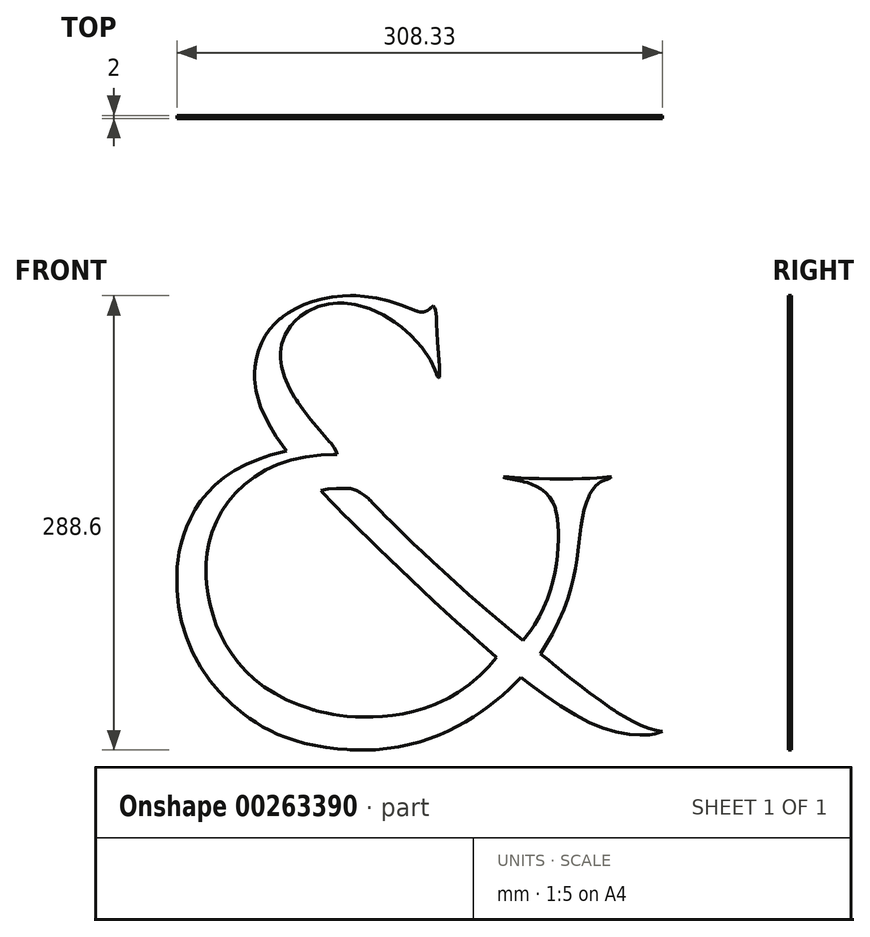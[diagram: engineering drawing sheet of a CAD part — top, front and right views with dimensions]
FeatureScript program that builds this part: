
annotation { "Feature Type Name" : "Feature", "Feature Type Description" : "" }
export const myFeature = defineFeature(function(context is Context, id is Id, definition is map)
    precondition{}
    {
        {
            var Q0;
            Q0=qCreatedBy(makeId("Front.planeOp"),FACE);
            var sketch = newSketch(context, id + "F0", { "sketchPlane" : qUnion([Q0])});
            skLineSegment(sketch, "E0.0", {"start": v(10.88, 98.57) * mm, "end": v(10.85, 99.35) * mm});
            skLineSegment(sketch, "E0.1", {"start": v(10.98, 95.31) * mm, "end": v(10.88, 98.57) * mm});
            skLineSegment(sketch, "E0.2", {"start": v(11, 93.74) * mm, "end": v(10.98, 95.31) * mm});
            skLineSegment(sketch, "E0.3", {"start": v(11, 93.23) * mm, "end": v(11, 93.74) * mm});
            skLineSegment(sketch, "E0.4", {"start": v(11, 93.13) * mm, "end": v(11, 93.23) * mm});
            skLineSegment(sketch, "E0.5", {"start": v(10.9, 92.6) * mm, "end": v(11, 93.13) * mm});
            skLineSegment(sketch, "E0.6", {"start": v(10.8, 92.45) * mm, "end": v(10.9, 92.6) * mm});
            skLineSegment(sketch, "E0.7", {"start": v(10.65, 92.35) * mm, "end": v(10.8, 92.45) * mm});
            skLineSegment(sketch, "E0.8", {"start": v(10.37, 92.3) * mm, "end": v(10.65, 92.35) * mm});
            skLineSegment(sketch, "E0.9", {"start": v(9.81, 93.06) * mm, "end": v(10.37, 92.3) * mm});
            skLineSegment(sketch, "E0.10", {"start": v(9.22, 94.33) * mm, "end": v(9.81, 93.06) * mm});
            skLineSegment(sketch, "E0.11", {"start": v(9.08, 94.75) * mm, "end": v(9.22, 94.33) * mm});
            skLineSegment(sketch, "E0.12", {"start": v(8.28, 97.07) * mm, "end": v(9.08, 94.75) * mm});
            skLineSegment(sketch, "E0.13", {"start": v(5.2, 103.48) * mm, "end": v(8.28, 97.07) * mm});
            skLineSegment(sketch, "E0.14", {"start": v(-0.18, 111.5) * mm, "end": v(5.2, 103.48) * mm});
            skLineSegment(sketch, "E0.15", {"start": v(-7.05, 118.97) * mm, "end": v(-0.18, 111.5) * mm});
            skLineSegment(sketch, "E0.16", {"start": v(-13.2, 124.31) * mm, "end": v(-7.05, 118.97) * mm});
            skLineSegment(sketch, "E0.17", {"start": v(-15.4, 125.94) * mm, "end": v(-13.2, 124.31) * mm});
            skLineSegment(sketch, "E0.18", {"start": v(-17.59, 127.57) * mm, "end": v(-15.4, 125.94) * mm});
            skLineSegment(sketch, "E0.19", {"start": v(-24.48, 131.9) * mm, "end": v(-17.59, 127.57) * mm});
            skLineSegment(sketch, "E0.20", {"start": v(-33.54, 136.2) * mm, "end": v(-24.48, 131.9) * mm});
            skLineSegment(sketch, "E0.21", {"start": v(-42.64, 138.83) * mm, "end": v(-33.54, 136.2) * mm});
            skLineSegment(sketch, "E0.22", {"start": v(-49.52, 139.73) * mm, "end": v(-42.64, 138.83) * mm});
            skLineSegment(sketch, "E0.23", {"start": v(-51.92, 139.73) * mm, "end": v(-49.52, 139.73) * mm});
            skLineSegment(sketch, "E0.24", {"start": v(-53.84, 139.73) * mm, "end": v(-51.92, 139.73) * mm});
            skLineSegment(sketch, "E0.25", {"start": v(-59.41, 139.14) * mm, "end": v(-53.84, 139.73) * mm});
            skLineSegment(sketch, "E0.26", {"start": v(-66.3, 137.37) * mm, "end": v(-59.41, 139.14) * mm});
            skLineSegment(sketch, "E0.27", {"start": v(-72.67, 134.4) * mm, "end": v(-66.3, 137.37) * mm});
            skLineSegment(sketch, "E0.28", {"start": v(-77.18, 131.36) * mm, "end": v(-72.67, 134.4) * mm});
            skLineSegment(sketch, "E0.29", {"start": v(-78.62, 130.14) * mm, "end": v(-77.18, 131.36) * mm});
            skLineSegment(sketch, "E0.30", {"start": v(-80, 128.93) * mm, "end": v(-78.62, 130.14) * mm});
            skLineSegment(sketch, "E0.31", {"start": v(-83.6, 125) * mm, "end": v(-80, 128.93) * mm});
            skLineSegment(sketch, "E0.32", {"start": v(-87.14, 119.37) * mm, "end": v(-83.6, 125) * mm});
            skLineSegment(sketch, "E0.33", {"start": v(-89.3, 113.17) * mm, "end": v(-87.14, 119.37) * mm});
            skLineSegment(sketch, "E0.34", {"start": v(-90, 108.1) * mm, "end": v(-89.3, 113.17) * mm});
            skLineSegment(sketch, "E0.35", {"start": v(-90, 106.33) * mm, "end": v(-90, 108.1) * mm});
            skLineSegment(sketch, "E0.36", {"start": v(-90, 104.52) * mm, "end": v(-90, 106.33) * mm});
            skLineSegment(sketch, "E0.37", {"start": v(-89.32, 99.47) * mm, "end": v(-90, 104.52) * mm});
            skLineSegment(sketch, "E0.38", {"start": v(-87.37, 92.57) * mm, "end": v(-89.32, 99.47) * mm});
            skLineSegment(sketch, "E0.39", {"start": v(-84.22, 85.42) * mm, "end": v(-87.37, 92.57) * mm});
            skLineSegment(sketch, "E0.40", {"start": v(-81.05, 79.78) * mm, "end": v(-84.22, 85.42) * mm});
            skLineSegment(sketch, "E0.41", {"start": v(-79.86, 77.94) * mm, "end": v(-81.05, 79.78) * mm});
            skLineSegment(sketch, "E0.42", {"start": v(-78.87, 76.43) * mm, "end": v(-79.86, 77.94) * mm});
            skLineSegment(sketch, "E0.43", {"start": v(-75.82, 72.14) * mm, "end": v(-78.87, 76.43) * mm});
            skLineSegment(sketch, "E0.44", {"start": v(-70.97, 65.81) * mm, "end": v(-75.82, 72.14) * mm});
            skLineSegment(sketch, "E0.45", {"start": v(-65.27, 58.9) * mm, "end": v(-70.97, 65.81) * mm});
            skLineSegment(sketch, "E0.46", {"start": v(-60.36, 53.25) * mm, "end": v(-65.27, 58.9) * mm});
            skLineSegment(sketch, "E0.47", {"start": v(-58.71, 51.43) * mm, "end": v(-60.36, 53.25) * mm});
            skLineSegment(sketch, "E0.48", {"start": v(-58, 50.6) * mm, "end": v(-58.71, 51.43) * mm});
            skLineSegment(sketch, "E0.49", {"start": v(-55.94, 47.76) * mm, "end": v(-58, 50.6) * mm});
            skLineSegment(sketch, "E0.50", {"start": v(-54.51, 44.91) * mm, "end": v(-55.94, 47.76) * mm});
            skLineSegment(sketch, "E0.51", {"start": v(-54.22, 43.46) * mm, "end": v(-54.51, 44.91) * mm});
            skLineSegment(sketch, "E0.52", {"start": v(-56.26, 43.49) * mm, "end": v(-54.22, 43.46) * mm});
            skLineSegment(sketch, "E0.53", {"start": v(-64.25, 43.15) * mm, "end": v(-56.26, 43.49) * mm});
            skLineSegment(sketch, "E0.54", {"start": v(-74.13, 41.94) * mm, "end": v(-64.25, 43.15) * mm});
            skLineSegment(sketch, "E0.55", {"start": v(-83.33, 39.88) * mm, "end": v(-74.13, 41.94) * mm});
            skLineSegment(sketch, "E0.56", {"start": v(-91.8, 37.03) * mm, "end": v(-83.33, 39.88) * mm});
            skLineSegment(sketch, "E0.57", {"start": v(-99.55, 33.45) * mm, "end": v(-91.8, 37.03) * mm});
            skLineSegment(sketch, "E0.58", {"start": v(-106.57, 29.22) * mm, "end": v(-99.55, 33.45) * mm});
            skLineSegment(sketch, "E0.59", {"start": v(-112.85, 24.4) * mm, "end": v(-106.57, 29.22) * mm});
            skLineSegment(sketch, "E0.60", {"start": v(-118.4, 19.1) * mm, "end": v(-112.85, 24.4) * mm});
            skLineSegment(sketch, "E0.61", {"start": v(-123.2, 13.36) * mm, "end": v(-118.4, 19.1) * mm});
            skLineSegment(sketch, "E0.62", {"start": v(-127.3, 7.27) * mm, "end": v(-123.2, 13.36) * mm});
            skLineSegment(sketch, "E0.63", {"start": v(-130.67, 0.92) * mm, "end": v(-127.3, 7.27) * mm});
            skLineSegment(sketch, "E0.64", {"start": v(-133.35, -5.63) * mm, "end": v(-130.67, 0.92) * mm});
            skLineSegment(sketch, "E0.65", {"start": v(-135.34, -12.3) * mm, "end": v(-133.35, -5.63) * mm});
            skLineSegment(sketch, "E0.66", {"start": v(-136.66, -19.03) * mm, "end": v(-135.34, -12.3) * mm});
            skLineSegment(sketch, "E0.67", {"start": v(-137.32, -25.7) * mm, "end": v(-136.66, -19.03) * mm});
            skLineSegment(sketch, "E0.68", {"start": v(-137.41, -30.7) * mm, "end": v(-137.32, -25.7) * mm});
            skLineSegment(sketch, "E0.69", {"start": v(-137.33, -32.4) * mm, "end": v(-137.41, -30.7) * mm});
            skLineSegment(sketch, "E0.70", {"start": v(-137.26, -34.04) * mm, "end": v(-137.33, -32.4) * mm});
            skLineSegment(sketch, "E0.71", {"start": v(-136.85, -38.9) * mm, "end": v(-137.26, -34.04) * mm});
            skLineSegment(sketch, "E0.72", {"start": v(-135.98, -45.36) * mm, "end": v(-136.85, -38.9) * mm});
            skLineSegment(sketch, "E0.73", {"start": v(-134.69, -51.86) * mm, "end": v(-135.98, -45.36) * mm});
            skLineSegment(sketch, "E0.74", {"start": v(-132.96, -58.32) * mm, "end": v(-134.69, -51.86) * mm});
            skLineSegment(sketch, "E0.75", {"start": v(-130.77, -64.71) * mm, "end": v(-132.96, -58.32) * mm});
            skLineSegment(sketch, "E0.76", {"start": v(-128.08, -71) * mm, "end": v(-130.77, -64.71) * mm});
            skLineSegment(sketch, "E0.77", {"start": v(-124.88, -77.12) * mm, "end": v(-128.08, -71) * mm});
            skLineSegment(sketch, "E0.78", {"start": v(-121.13, -83.06) * mm, "end": v(-124.88, -77.12) * mm});
            skLineSegment(sketch, "E0.79", {"start": v(-116.82, -88.76) * mm, "end": v(-121.13, -83.06) * mm});
            skLineSegment(sketch, "E0.80", {"start": v(-111.92, -94.2) * mm, "end": v(-116.82, -88.76) * mm});
            skLineSegment(sketch, "E0.81", {"start": v(-106.42, -99.3) * mm, "end": v(-111.92, -94.2) * mm});
            skLineSegment(sketch, "E0.82", {"start": v(-100.3, -104.05) * mm, "end": v(-106.42, -99.3) * mm});
            skLineSegment(sketch, "E0.83", {"start": v(-93.54, -108.39) * mm, "end": v(-100.3, -104.05) * mm});
            skLineSegment(sketch, "E0.84", {"start": v(-86.15, -112.3) * mm, "end": v(-93.54, -108.39) * mm});
            skLineSegment(sketch, "E0.85", {"start": v(-78.13, -115.7) * mm, "end": v(-86.15, -112.3) * mm});
            skLineSegment(sketch, "E0.86", {"start": v(-71.6, -117.99) * mm, "end": v(-78.13, -115.7) * mm});
            skLineSegment(sketch, "E0.87", {"start": v(-69.37, -118.64) * mm, "end": v(-71.6, -117.99) * mm});
            skLineSegment(sketch, "E0.88", {"start": v(-68.77, -118.82) * mm, "end": v(-69.37, -118.64) * mm});
            skLineSegment(sketch, "E0.89", {"start": v(-67, -119.3) * mm, "end": v(-68.77, -118.82) * mm});
            skLineSegment(sketch, "E0.90", {"start": v(-64.11, -120.03) * mm, "end": v(-67, -119.3) * mm});
            skLineSegment(sketch, "E0.91", {"start": v(-60.69, -120.79) * mm, "end": v(-64.11, -120.03) * mm});
            skLineSegment(sketch, "E0.92", {"start": v(-56.78, -121.52) * mm, "end": v(-60.69, -120.79) * mm});
            skLineSegment(sketch, "E0.93", {"start": v(-52.42, -122.2) * mm, "end": v(-56.78, -121.52) * mm});
            skLineSegment(sketch, "E0.94", {"start": v(-47.64, -122.76) * mm, "end": v(-52.42, -122.2) * mm});
            skLineSegment(sketch, "E0.95", {"start": v(-42.48, -123.17) * mm, "end": v(-47.64, -122.76) * mm});
            skLineSegment(sketch, "E0.96", {"start": v(-36.98, -123.38) * mm, "end": v(-42.48, -123.17) * mm});
            skLineSegment(sketch, "E0.97", {"start": v(-31.17, -123.34) * mm, "end": v(-36.98, -123.38) * mm});
            skLineSegment(sketch, "E0.98", {"start": v(-25.08, -123) * mm, "end": v(-31.17, -123.34) * mm});
            skLineSegment(sketch, "E0.99", {"start": v(-18.75, -122.31) * mm, "end": v(-25.08, -123) * mm});
            skLineSegment(sketch, "E0.100", {"start": v(-12.22, -121.24) * mm, "end": v(-18.75, -122.31) * mm});
            skLineSegment(sketch, "E0.101", {"start": v(-5.53, -119.72) * mm, "end": v(-12.22, -121.24) * mm});
            skLineSegment(sketch, "E0.102", {"start": v(1.29, -117.71) * mm, "end": v(-5.53, -119.72) * mm});
            skLineSegment(sketch, "E0.103", {"start": v(8.15, -115.18) * mm, "end": v(1.29, -117.71) * mm});
            skLineSegment(sketch, "E0.104", {"start": v(13.39, -112.9) * mm, "end": v(8.15, -115.18) * mm});
            skLineSegment(sketch, "E0.105", {"start": v(15.12, -112.04) * mm, "end": v(13.39, -112.9) * mm});
            skLineSegment(sketch, "E0.106", {"start": v(17.12, -111.06) * mm, "end": v(15.12, -112.04) * mm});
            skLineSegment(sketch, "E0.107", {"start": v(22.76, -107.77) * mm, "end": v(17.12, -111.06) * mm});
            skLineSegment(sketch, "E0.108", {"start": v(30.13, -102.6) * mm, "end": v(22.76, -107.77) * mm});
            skLineSegment(sketch, "E0.109", {"start": v(37.13, -96.55) * mm, "end": v(30.13, -102.6) * mm});
            skLineSegment(sketch, "E0.110", {"start": v(42.07, -91.48) * mm, "end": v(37.13, -96.55) * mm});
            skLineSegment(sketch, "E0.111", {"start": v(47.23, -85.34) * mm, "end": v(42.07, -91.48) * mm});
            skLineSegment(sketch, "E0.112", {"start": v(41.28, -80.18) * mm, "end": v(47.23, -85.34) * mm});
            skLineSegment(sketch, "E0.113", {"start": v(36.16, -75.67) * mm, "end": v(41.28, -80.18) * mm});
            skLineSegment(sketch, "E0.114", {"start": v(29.1, -69.4) * mm, "end": v(36.16, -75.67) * mm});
            skLineSegment(sketch, "E0.115", {"start": v(21.91, -62.9) * mm, "end": v(29.1, -69.4) * mm});
            skLineSegment(sketch, "E0.116", {"start": v(14.63, -56.26) * mm, "end": v(21.91, -62.9) * mm});
            skLineSegment(sketch, "E0.117", {"start": v(7.31, -49.5) * mm, "end": v(14.63, -56.26) * mm});
            skLineSegment(sketch, "E0.118", {"start": v(0.03, -42.72) * mm, "end": v(7.31, -49.5) * mm});
            skLineSegment(sketch, "E0.119", {"start": v(-7.17, -35.95) * mm, "end": v(0.03, -42.72) * mm});
            skLineSegment(sketch, "E0.120", {"start": v(-14.22, -29.27) * mm, "end": v(-7.17, -35.95) * mm});
            skLineSegment(sketch, "E0.121", {"start": v(-21.06, -22.73) * mm, "end": v(-14.22, -29.27) * mm});
            skLineSegment(sketch, "E0.122", {"start": v(-27.64, -16.4) * mm, "end": v(-21.06, -22.73) * mm});
            skLineSegment(sketch, "E0.123", {"start": v(-33.9, -10.32) * mm, "end": v(-27.64, -16.4) * mm});
            skLineSegment(sketch, "E0.124", {"start": v(-39.77, -4.57) * mm, "end": v(-33.9, -10.32) * mm});
            skLineSegment(sketch, "E0.125", {"start": v(-45.2, 0.8) * mm, "end": v(-39.77, -4.57) * mm});
            skLineSegment(sketch, "E0.126", {"start": v(-50.13, 5.7) * mm, "end": v(-45.2, 0.8) * mm});
            skLineSegment(sketch, "E0.127", {"start": v(-54.5, 10.12) * mm, "end": v(-50.13, 5.7) * mm});
            skLineSegment(sketch, "E0.128", {"start": v(-57.31, 13) * mm, "end": v(-54.5, 10.12) * mm});
            skLineSegment(sketch, "E0.129", {"start": v(-58.24, 13.95) * mm, "end": v(-57.31, 13) * mm});
            skLineSegment(sketch, "E0.130", {"start": v(-58.96, 14.7) * mm, "end": v(-58.24, 13.95) * mm});
            skLineSegment(sketch, "E0.131", {"start": v(-61.08, 16.96) * mm, "end": v(-58.96, 14.7) * mm});
            skLineSegment(sketch, "E0.132", {"start": v(-63.16, 19.3) * mm, "end": v(-61.08, 16.96) * mm});
            skLineSegment(sketch, "E0.133", {"start": v(-64.3, 20.7) * mm, "end": v(-63.16, 19.3) * mm});
            skLineSegment(sketch, "E0.134", {"start": v(-64.17, 20.74) * mm, "end": v(-64.3, 20.7) * mm});
            skLineSegment(sketch, "E0.135", {"start": v(-59.7, 21.46) * mm, "end": v(-64.17, 20.74) * mm});
            skLineSegment(sketch, "E0.136", {"start": v(-54.54, 21.77) * mm, "end": v(-59.7, 21.46) * mm});
            skLineSegment(sketch, "E0.137", {"start": v(-52.81, 21.8) * mm, "end": v(-54.54, 21.77) * mm});
            skLineSegment(sketch, "E0.138", {"start": v(-52.06, 21.8) * mm, "end": v(-52.81, 21.8) * mm});
            skLineSegment(sketch, "E0.139", {"start": v(-49.92, 21.86) * mm, "end": v(-52.06, 21.8) * mm});
            skLineSegment(sketch, "E0.140", {"start": v(-47.47, 21.87) * mm, "end": v(-49.92, 21.86) * mm});
            skLineSegment(sketch, "E0.141", {"start": v(-45.4, 21.73) * mm, "end": v(-47.47, 21.87) * mm});
            skLineSegment(sketch, "E0.142", {"start": v(-43.53, 21.37) * mm, "end": v(-45.4, 21.73) * mm});
            skLineSegment(sketch, "E0.143", {"start": v(-41.6, 20.68) * mm, "end": v(-43.53, 21.37) * mm});
            skLineSegment(sketch, "E0.144", {"start": v(-39.37, 19.47) * mm, "end": v(-41.6, 20.68) * mm});
            skLineSegment(sketch, "E0.145", {"start": v(-36.64, 17.5) * mm, "end": v(-39.37, 19.47) * mm});
            skLineSegment(sketch, "E0.146", {"start": v(-34.2, 15.36) * mm, "end": v(-36.64, 17.5) * mm});
            skLineSegment(sketch, "E0.147", {"start": v(-33.43, 14.62) * mm, "end": v(-34.2, 15.36) * mm});
            skLineSegment(sketch, "E0.148", {"start": v(-32.94, 14.14) * mm, "end": v(-33.43, 14.62) * mm});
            skLineSegment(sketch, "E0.149", {"start": v(-31.45, 12.65) * mm, "end": v(-32.94, 14.14) * mm});
            skLineSegment(sketch, "E0.150", {"start": v(-29.08, 10.26) * mm, "end": v(-31.45, 12.65) * mm});
            skLineSegment(sketch, "E0.151", {"start": v(-26.33, 7.45) * mm, "end": v(-29.08, 10.26) * mm});
            skLineSegment(sketch, "E0.152", {"start": v(-23.17, 4.22) * mm, "end": v(-26.33, 7.45) * mm});
            skLineSegment(sketch, "E0.153", {"start": v(-19.55, 0.56) * mm, "end": v(-23.17, 4.22) * mm});
            skLineSegment(sketch, "E0.154", {"start": v(-15.45, -3.54) * mm, "end": v(-19.55, 0.56) * mm});
            skLineSegment(sketch, "E0.155", {"start": v(-10.84, -8.08) * mm, "end": v(-15.45, -3.54) * mm});
            skLineSegment(sketch, "E0.156", {"start": v(-5.68, -13.08) * mm, "end": v(-10.84, -8.08) * mm});
            skLineSegment(sketch, "E0.157", {"start": v(0.07, -18.55) * mm, "end": v(-5.68, -13.08) * mm});
            skLineSegment(sketch, "E0.158", {"start": v(6.43, -24.5) * mm, "end": v(0.07, -18.55) * mm});
            skLineSegment(sketch, "E0.159", {"start": v(13.44, -30.93) * mm, "end": v(6.43, -24.5) * mm});
            skLineSegment(sketch, "E0.160", {"start": v(21.14, -37.87) * mm, "end": v(13.44, -30.93) * mm});
            skLineSegment(sketch, "E0.161", {"start": v(29.56, -45.32) * mm, "end": v(21.14, -37.87) * mm});
            skLineSegment(sketch, "E0.162", {"start": v(38.74, -53.3) * mm, "end": v(29.56, -45.32) * mm});
            skLineSegment(sketch, "E0.163", {"start": v(48.7, -61.8) * mm, "end": v(38.74, -53.3) * mm});
            skLineSegment(sketch, "E0.164", {"start": v(56.8, -68.62) * mm, "end": v(48.7, -61.8) * mm});
            skLineSegment(sketch, "E0.165", {"start": v(64.08, -74.69) * mm, "end": v(56.8, -68.62) * mm});
            skLineSegment(sketch, "E0.166", {"start": v(68.66, -68.66) * mm, "end": v(64.08, -74.69) * mm});
            skLineSegment(sketch, "E0.167", {"start": v(71.3, -64.77) * mm, "end": v(68.66, -68.66) * mm});
            skLineSegment(sketch, "E0.168", {"start": v(74.42, -59.44) * mm, "end": v(71.3, -64.77) * mm});
            skLineSegment(sketch, "E0.169", {"start": v(77.14, -53.93) * mm, "end": v(74.42, -59.44) * mm});
            skLineSegment(sketch, "E0.170", {"start": v(79.45, -48.33) * mm, "end": v(77.14, -53.93) * mm});
            skLineSegment(sketch, "E0.171", {"start": v(81.4, -42.67) * mm, "end": v(79.45, -48.33) * mm});
            skLineSegment(sketch, "E0.172", {"start": v(82.98, -37.03) * mm, "end": v(81.4, -42.67) * mm});
            skLineSegment(sketch, "E0.173", {"start": v(84.25, -31.43) * mm, "end": v(82.98, -37.03) * mm});
            skLineSegment(sketch, "E0.174", {"start": v(85.21, -25.93) * mm, "end": v(84.25, -31.43) * mm});
            skLineSegment(sketch, "E0.175", {"start": v(85.9, -20.58) * mm, "end": v(85.21, -25.93) * mm});
            skLineSegment(sketch, "E0.176", {"start": v(86.32, -15.42) * mm, "end": v(85.9, -20.58) * mm});
            skLineSegment(sketch, "E0.177", {"start": v(86.51, -10.5) * mm, "end": v(86.32, -15.42) * mm});
            skLineSegment(sketch, "E0.178", {"start": v(86.49, -5.87) * mm, "end": v(86.51, -10.5) * mm});
            skLineSegment(sketch, "E0.179", {"start": v(86.26, -1.55) * mm, "end": v(86.49, -5.87) * mm});
            skLineSegment(sketch, "E0.180", {"start": v(85.85, 2.4) * mm, "end": v(86.26, -1.55) * mm});
            skLineSegment(sketch, "E0.181", {"start": v(85.28, 5.95) * mm, "end": v(85.85, 2.4) * mm});
            skLineSegment(sketch, "E0.182", {"start": v(84.75, 8.32) * mm, "end": v(85.28, 5.95) * mm});
            skLineSegment(sketch, "E0.183", {"start": v(84.51, 9.14) * mm, "end": v(84.75, 8.32) * mm});
            skLineSegment(sketch, "E0.184", {"start": v(84.2, 10.22) * mm, "end": v(84.51, 9.14) * mm});
            skLineSegment(sketch, "E0.185", {"start": v(82.98, 13.1) * mm, "end": v(84.2, 10.22) * mm});
            skLineSegment(sketch, "E0.186", {"start": v(80.91, 16.38) * mm, "end": v(82.98, 13.1) * mm});
            skLineSegment(sketch, "E0.187", {"start": v(78.38, 19.17) * mm, "end": v(80.91, 16.38) * mm});
            skLineSegment(sketch, "E0.188", {"start": v(75.58, 21.41) * mm, "end": v(78.38, 19.17) * mm});
            skLineSegment(sketch, "E0.189", {"start": v(72.65, 23.18) * mm, "end": v(75.58, 21.41) * mm});
            skLineSegment(sketch, "E0.190", {"start": v(69.7, 24.54) * mm, "end": v(72.65, 23.18) * mm});
            skLineSegment(sketch, "E0.191", {"start": v(66.84, 25.53) * mm, "end": v(69.7, 24.54) * mm});
            skLineSegment(sketch, "E0.192", {"start": v(64.76, 26.08) * mm, "end": v(66.84, 25.53) * mm});
            skLineSegment(sketch, "E0.193", {"start": v(63.98, 26.25) * mm, "end": v(64.76, 26.08) * mm});
            skLineSegment(sketch, "E0.194", {"start": v(54.4, 28.1) * mm, "end": v(63.98, 26.25) * mm});
            skLineSegment(sketch, "E0.195", {"start": v(54.07, 28.16) * mm, "end": v(54.4, 28.1) * mm});
            skLineSegment(sketch, "E0.196", {"start": v(52.96, 28.48) * mm, "end": v(54.07, 28.16) * mm});
            skLineSegment(sketch, "E0.197", {"start": v(52, 28.91) * mm, "end": v(52.96, 28.48) * mm});
            skLineSegment(sketch, "E0.198", {"start": v(51.6, 29.2) * mm, "end": v(52, 28.91) * mm});
            skLineSegment(sketch, "E0.199", {"start": v(52.17, 29.26) * mm, "end": v(51.6, 29.2) * mm});
            skLineSegment(sketch, "E0.200", {"start": v(52.38, 29.26) * mm, "end": v(52.17, 29.26) * mm});
            skLineSegment(sketch, "E0.201", {"start": v(52.46, 29.26) * mm, "end": v(52.38, 29.26) * mm});
            skLineSegment(sketch, "E0.202", {"start": v(53.11, 29.21) * mm, "end": v(52.46, 29.26) * mm});
            skLineSegment(sketch, "E0.203", {"start": v(55.28, 29.06) * mm, "end": v(53.11, 29.21) * mm});
            skLineSegment(sketch, "E0.204", {"start": v(58.48, 28.83) * mm, "end": v(55.28, 29.06) * mm});
            skLineSegment(sketch, "E0.205", {"start": v(62.7, 28.56) * mm, "end": v(58.48, 28.83) * mm});
            skLineSegment(sketch, "E0.206", {"start": v(67.91, 28.3) * mm, "end": v(62.7, 28.56) * mm});
            skLineSegment(sketch, "E0.207", {"start": v(74.12, 28.07) * mm, "end": v(67.91, 28.3) * mm});
            skLineSegment(sketch, "E0.208", {"start": v(81.3, 27.9) * mm, "end": v(74.12, 28.07) * mm});
            skLineSegment(sketch, "E0.209", {"start": v(-86.43, -136.35) * mm, "end": v(-80.75, -138.26) * mm});
            skLineSegment(sketch, "E0.210", {"start": v(-91.73, -134.24) * mm, "end": v(-86.43, -136.35) * mm});
            skLineSegment(sketch, "E0.211", {"start": v(-96.69, -131.94) * mm, "end": v(-91.73, -134.24) * mm});
            skLineSegment(sketch, "E0.212", {"start": v(-101.32, -129.48) * mm, "end": v(-96.69, -131.94) * mm});
            skLineSegment(sketch, "E0.213", {"start": v(-105.67, -126.86) * mm, "end": v(-101.32, -129.48) * mm});
            skLineSegment(sketch, "E0.214", {"start": v(-109.76, -124.12) * mm, "end": v(-105.67, -126.86) * mm});
            skLineSegment(sketch, "E0.215", {"start": v(-113.61, -121.26) * mm, "end": v(-109.76, -124.12) * mm});
            skLineSegment(sketch, "E0.216", {"start": v(-117.26, -118.3) * mm, "end": v(-113.61, -121.26) * mm});
            skLineSegment(sketch, "E0.217", {"start": v(-120.72, -115.24) * mm, "end": v(-117.26, -118.3) * mm});
            skLineSegment(sketch, "E0.218", {"start": v(-124.04, -112.11) * mm, "end": v(-120.72, -115.24) * mm});
            skLineSegment(sketch, "E0.219", {"start": v(-126.43, -109.75) * mm, "end": v(-124.04, -112.11) * mm});
            skLineSegment(sketch, "E0.220", {"start": v(-127.2, -108.95) * mm, "end": v(-126.43, -109.75) * mm});
            skLineSegment(sketch, "E0.221", {"start": v(-129.13, -106.97) * mm, "end": v(-127.2, -108.95) * mm});
            skLineSegment(sketch, "E0.222", {"start": v(-134.6, -100.5) * mm, "end": v(-129.13, -106.97) * mm});
            skLineSegment(sketch, "E0.223", {"start": v(-140.82, -91.6) * mm, "end": v(-134.6, -100.5) * mm});
            skLineSegment(sketch, "E0.224", {"start": v(-145.85, -82.36) * mm, "end": v(-140.82, -91.6) * mm});
            skLineSegment(sketch, "E0.225", {"start": v(-149.79, -72.82) * mm, "end": v(-145.85, -82.36) * mm});
            skLineSegment(sketch, "E0.226", {"start": v(-152.7, -63) * mm, "end": v(-149.79, -72.82) * mm});
            skLineSegment(sketch, "E0.227", {"start": v(-154.62, -52.94) * mm, "end": v(-152.7, -63) * mm});
            skLineSegment(sketch, "E0.228", {"start": v(-155.63, -42.65) * mm, "end": v(-154.62, -52.94) * mm});
            skLineSegment(sketch, "E0.229", {"start": v(-155.83, -34.86) * mm, "end": v(-155.63, -42.65) * mm});
            skLineSegment(sketch, "E0.230", {"start": v(-155.75, -32.3) * mm, "end": v(-155.83, -34.86) * mm});
            skLineSegment(sketch, "E0.231", {"start": v(-155.73, -31.26) * mm, "end": v(-155.75, -32.3) * mm});
            skLineSegment(sketch, "E0.232", {"start": v(-155.54, -28.12) * mm, "end": v(-155.73, -31.26) * mm});
            skLineSegment(sketch, "E0.233", {"start": v(-155.06, -23.5) * mm, "end": v(-155.54, -28.12) * mm});
            skLineSegment(sketch, "E0.234", {"start": v(-154.3, -18.57) * mm, "end": v(-155.06, -23.5) * mm});
            skLineSegment(sketch, "E0.235", {"start": v(-153.17, -13.38) * mm, "end": v(-154.3, -18.57) * mm});
            skLineSegment(sketch, "E0.236", {"start": v(-151.66, -8.02) * mm, "end": v(-153.17, -13.38) * mm});
            skLineSegment(sketch, "E0.237", {"start": v(-149.7, -2.55) * mm, "end": v(-151.66, -8.02) * mm});
            skLineSegment(sketch, "E0.238", {"start": v(-147.23, 2.96) * mm, "end": v(-149.7, -2.55) * mm});
            skLineSegment(sketch, "E0.239", {"start": v(-144.24, 8.43) * mm, "end": v(-147.23, 2.96) * mm});
            skLineSegment(sketch, "E0.240", {"start": v(-140.65, 13.8) * mm, "end": v(-144.24, 8.43) * mm});
            skLineSegment(sketch, "E0.241", {"start": v(-136.42, 19.03) * mm, "end": v(-140.65, 13.8) * mm});
            skLineSegment(sketch, "E0.242", {"start": v(-131.48, 24.03) * mm, "end": v(-136.42, 19.03) * mm});
            skLineSegment(sketch, "E0.243", {"start": v(-125.8, 28.76) * mm, "end": v(-131.48, 24.03) * mm});
            skLineSegment(sketch, "E0.244", {"start": v(-119.27, 33.15) * mm, "end": v(-125.8, 28.76) * mm});
            skLineSegment(sketch, "E0.245", {"start": v(-111.86, 37.13) * mm, "end": v(-119.27, 33.15) * mm});
            skLineSegment(sketch, "E0.246", {"start": v(-103.44, 40.66) * mm, "end": v(-111.86, 37.13) * mm});
            skLineSegment(sketch, "E0.247", {"start": v(-96.4, 42.98) * mm, "end": v(-103.44, 40.66) * mm});
            skLineSegment(sketch, "E0.248", {"start": v(-86, 45.75) * mm, "end": v(-96.4, 42.98) * mm});
            skLineSegment(sketch, "E0.249", {"start": v(-92.77, 54.99) * mm, "end": v(-86, 45.75) * mm});
            skLineSegment(sketch, "E0.250", {"start": v(-97.74, 63.1) * mm, "end": v(-92.77, 54.99) * mm});
            skLineSegment(sketch, "E0.251", {"start": v(-102.56, 73.6) * mm, "end": v(-97.74, 63.1) * mm});
            skLineSegment(sketch, "E0.252", {"start": v(-105.42, 83.9) * mm, "end": v(-102.56, 73.6) * mm});
            skLineSegment(sketch, "E0.253", {"start": v(-106.35, 91.42) * mm, "end": v(-105.42, 83.9) * mm});
            skLineSegment(sketch, "E0.254", {"start": v(-106.35, 93.83) * mm, "end": v(-106.35, 91.42) * mm});
            skLineSegment(sketch, "E0.255", {"start": v(-106.35, 95.19) * mm, "end": v(-106.35, 93.83) * mm});
            skLineSegment(sketch, "E0.256", {"start": v(-106.08, 99.38) * mm, "end": v(-106.35, 95.19) * mm});
            skLineSegment(sketch, "E0.257", {"start": v(-105.27, 104.7) * mm, "end": v(-106.08, 99.38) * mm});
            skLineSegment(sketch, "E0.258", {"start": v(-103.95, 109.64) * mm, "end": v(-105.27, 104.7) * mm});
            skLineSegment(sketch, "E0.259", {"start": v(-2.63, 134.2) * mm, "end": v(-3.42, 134.44) * mm});
            skLineSegment(sketch, "E0.260", {"start": v(-1.47, 133.96) * mm, "end": v(-2.63, 134.2) * mm});
            skLineSegment(sketch, "E0.261", {"start": v(-0.1, 133.86) * mm, "end": v(-1.47, 133.96) * mm});
            skLineSegment(sketch, "E0.262", {"start": v(0.7, 133.96) * mm, "end": v(-0.1, 133.86) * mm});
            skLineSegment(sketch, "E0.263", {"start": v(1.83, 134.14) * mm, "end": v(0.7, 133.96) * mm});
            skLineSegment(sketch, "E0.264", {"start": v(3.45, 135) * mm, "end": v(1.83, 134.14) * mm});
            skLineSegment(sketch, "E0.265", {"start": v(4.6, 135.85) * mm, "end": v(3.45, 135) * mm});
            skLineSegment(sketch, "E0.266", {"start": v(5.44, 136.56) * mm, "end": v(4.6, 135.85) * mm});
            skLineSegment(sketch, "E0.267", {"start": v(5.84, 136.9) * mm, "end": v(5.44, 136.56) * mm});
            skLineSegment(sketch, "E0.268", {"start": v(5.92, 136.96) * mm, "end": v(5.84, 136.9) * mm});
            skLineSegment(sketch, "E0.269", {"start": v(6.08, 137.09) * mm, "end": v(5.92, 136.96) * mm});
            skLineSegment(sketch, "E0.270", {"start": v(6.65, 137.48) * mm, "end": v(6.08, 137.09) * mm});
            skLineSegment(sketch, "E0.271", {"start": v(9.18, 128.45) * mm, "end": v(9.08, 130.67) * mm});
            skLineSegment(sketch, "E0.272", {"start": v(9.19, 127.13) * mm, "end": v(9.18, 128.45) * mm});
            skLineSegment(sketch, "E0.273", {"start": v(9.19, 126.52) * mm, "end": v(9.19, 127.13) * mm});
            skLineSegment(sketch, "E0.274", {"start": v(9.82, 115.32) * mm, "end": v(9.19, 126.52) * mm});
            skLineSegment(sketch, "E0.275", {"start": v(9.08, 130.67) * mm, "end": v(8.84, 133) * mm});
            skLineSegment(sketch, "E0.276", {"start": v(8.84, 133) * mm, "end": v(8.41, 135.17) * mm});
            skLineSegment(sketch, "E0.277", {"start": v(8.41, 135.17) * mm, "end": v(7.84, 136.8) * mm});
            skLineSegment(sketch, "E0.278", {"start": v(7.84, 136.8) * mm, "end": v(7.34, 137.6) * mm});
            skLineSegment(sketch, "E0.279", {"start": v(7.34, 137.6) * mm, "end": v(7.16, 137.74) * mm});
            skLineSegment(sketch, "E0.280", {"start": v(7.16, 137.74) * mm, "end": v(6.65, 137.48) * mm});
            skLineSegment(sketch, "E0.281", {"start": v(-3.42, 134.44) * mm, "end": v(-3.76, 134.57) * mm});
            skLineSegment(sketch, "E0.282", {"start": v(-3.76, 134.57) * mm, "end": v(-13.38, 138.25) * mm});
            skLineSegment(sketch, "E0.283", {"start": v(-13.38, 138.25) * mm, "end": v(-15.29, 138.98) * mm});
            skLineSegment(sketch, "E0.284", {"start": v(-15.29, 138.98) * mm, "end": v(-21.22, 140.89) * mm});
            skLineSegment(sketch, "E0.285", {"start": v(-21.22, 140.89) * mm, "end": v(-28.96, 142.78) * mm});
            skLineSegment(sketch, "E0.286", {"start": v(-28.96, 142.78) * mm, "end": v(-36.5, 143.92) * mm});
            skLineSegment(sketch, "E0.287", {"start": v(-36.5, 143.92) * mm, "end": v(-41.94, 144.3) * mm});
            skLineSegment(sketch, "E0.288", {"start": v(-41.94, 144.3) * mm, "end": v(-43.7, 144.3) * mm});
            skLineSegment(sketch, "E0.289", {"start": v(-43.7, 144.3) * mm, "end": v(-45.43, 144.3) * mm});
            skLineSegment(sketch, "E0.290", {"start": v(-45.43, 144.3) * mm, "end": v(-50.7, 144.07) * mm});
            skLineSegment(sketch, "E0.291", {"start": v(-50.7, 144.07) * mm, "end": v(-57.4, 143.39) * mm});
            skLineSegment(sketch, "E0.292", {"start": v(-57.4, 143.39) * mm, "end": v(-63.7, 142.26) * mm});
            skLineSegment(sketch, "E0.293", {"start": v(-63.7, 142.26) * mm, "end": v(-69.6, 140.7) * mm});
            skLineSegment(sketch, "E0.294", {"start": v(-69.6, 140.7) * mm, "end": v(-75.12, 138.71) * mm});
            skLineSegment(sketch, "E0.295", {"start": v(-75.12, 138.71) * mm, "end": v(-80.27, 136.3) * mm});
            skLineSegment(sketch, "E0.296", {"start": v(-80.27, 136.3) * mm, "end": v(-85.1, 133.45) * mm});
            skLineSegment(sketch, "E0.297", {"start": v(-85.1, 133.45) * mm, "end": v(-88.45, 131.08) * mm});
            skLineSegment(sketch, "E0.298", {"start": v(-88.45, 131.08) * mm, "end": v(-89.47, 130.25) * mm});
            skLineSegment(sketch, "E0.299", {"start": v(-89.47, 130.25) * mm, "end": v(-90.47, 129.43) * mm});
            skLineSegment(sketch, "E0.300", {"start": v(-90.47, 129.43) * mm, "end": v(-93.42, 126.66) * mm});
            skLineSegment(sketch, "E0.301", {"start": v(-93.42, 126.66) * mm, "end": v(-96.88, 122.76) * mm});
            skLineSegment(sketch, "E0.302", {"start": v(-96.88, 122.76) * mm, "end": v(-99.76, 118.65) * mm});
            skLineSegment(sketch, "E0.303", {"start": v(-99.76, 118.65) * mm, "end": v(-102.11, 114.29) * mm});
            skLineSegment(sketch, "E0.304", {"start": v(-102.11, 114.29) * mm, "end": v(-103.95, 109.64) * mm});
            skLineSegment(sketch, "E0.305", {"start": v(-80.75, -138.26) * mm, "end": v(-74.67, -139.96) * mm});
            skLineSegment(sketch, "E0.306", {"start": v(-74.67, -139.96) * mm, "end": v(-68.15, -141.4) * mm});
            skLineSegment(sketch, "E0.307", {"start": v(-68.15, -141.4) * mm, "end": v(-61.17, -142.6) * mm});
            skLineSegment(sketch, "E0.308", {"start": v(-61.17, -142.6) * mm, "end": v(-53.68, -143.5) * mm});
            skLineSegment(sketch, "E0.309", {"start": v(10.85, 99.35) * mm, "end": v(9.82, 115.32) * mm});
            skLineSegment(sketch, "E0.310", {"start": v(-53.68, -143.5) * mm, "end": v(-47.7, -143.99) * mm});
            skLineSegment(sketch, "E0.311", {"start": v(-47.7, -143.99) * mm, "end": v(-45.71, -144.1) * mm});
            skLineSegment(sketch, "E0.312", {"start": v(-45.71, -144.1) * mm, "end": v(-43.7, -144.2) * mm});
            skLineSegment(sketch, "E0.313", {"start": v(-43.7, -144.2) * mm, "end": v(-37.59, -144.3) * mm});
            skLineSegment(sketch, "E0.314", {"start": v(-37.59, -144.3) * mm, "end": v(-29.73, -144.04) * mm});
            skLineSegment(sketch, "E0.315", {"start": v(-29.73, -144.04) * mm, "end": v(-22.23, -143.36) * mm});
            skLineSegment(sketch, "E0.316", {"start": v(-22.23, -143.36) * mm, "end": v(-15.03, -142.28) * mm});
            skLineSegment(sketch, "E0.317", {"start": v(-15.03, -142.28) * mm, "end": v(-8.13, -140.84) * mm});
            skLineSegment(sketch, "E0.318", {"start": v(-8.13, -140.84) * mm, "end": v(-1.52, -139.07) * mm});
            skLineSegment(sketch, "E0.319", {"start": v(-1.52, -139.07) * mm, "end": v(4.82, -137) * mm});
            skLineSegment(sketch, "E0.320", {"start": v(4.82, -137) * mm, "end": v(10.89, -134.65) * mm});
            skLineSegment(sketch, "E0.321", {"start": v(10.89, -134.65) * mm, "end": v(16.7, -132.06) * mm});
            skLineSegment(sketch, "E0.322", {"start": v(16.7, -132.06) * mm, "end": v(22.25, -129.26) * mm});
            skLineSegment(sketch, "E0.323", {"start": v(22.25, -129.26) * mm, "end": v(27.56, -126.28) * mm});
            skLineSegment(sketch, "E0.324", {"start": v(27.56, -126.28) * mm, "end": v(32.63, -123.16) * mm});
            skLineSegment(sketch, "E0.325", {"start": v(32.63, -123.16) * mm, "end": v(37.47, -119.91) * mm});
            skLineSegment(sketch, "E0.326", {"start": v(37.47, -119.91) * mm, "end": v(42.09, -116.58) * mm});
            skLineSegment(sketch, "E0.327", {"start": v(42.09, -116.58) * mm, "end": v(46.5, -113.18) * mm});
            skLineSegment(sketch, "E0.328", {"start": v(46.5, -113.18) * mm, "end": v(49.64, -110.64) * mm});
            skLineSegment(sketch, "E0.329", {"start": v(49.64, -110.64) * mm, "end": v(50.67, -109.77) * mm});
            skLineSegment(sketch, "E0.330", {"start": v(50.67, -109.77) * mm, "end": v(51.08, -109.43) * mm});
            skLineSegment(sketch, "E0.331", {"start": v(51.08, -109.43) * mm, "end": v(52.34, -108.32) * mm});
            skLineSegment(sketch, "E0.332", {"start": v(52.34, -108.32) * mm, "end": v(54.4, -106.44) * mm});
            skLineSegment(sketch, "E0.333", {"start": v(54.4, -106.44) * mm, "end": v(56.73, -104.21) * mm});
            skLineSegment(sketch, "E0.334", {"start": v(56.73, -104.21) * mm, "end": v(58.65, -102.34) * mm});
            skLineSegment(sketch, "E0.335", {"start": v(58.65, -102.34) * mm, "end": v(62.78, -98.22) * mm});
            skLineSegment(sketch, "E0.336", {"start": v(62.78, -98.22) * mm, "end": v(69.45, -103.23) * mm});
            skLineSegment(sketch, "E0.337", {"start": v(69.45, -103.23) * mm, "end": v(77.72, -109.25) * mm});
            skLineSegment(sketch, "E0.338", {"start": v(77.72, -109.25) * mm, "end": v(87.82, -116.2) * mm});
            skLineSegment(sketch, "E0.339", {"start": v(87.82, -116.2) * mm, "end": v(97.2, -121.98) * mm});
            skLineSegment(sketch, "E0.340", {"start": v(97.2, -121.98) * mm, "end": v(106.05, -126.64) * mm});
            skLineSegment(sketch, "E0.341", {"start": v(106.05, -126.64) * mm, "end": v(114.56, -130.2) * mm});
            skLineSegment(sketch, "E0.342", {"start": v(114.56, -130.2) * mm, "end": v(122.97, -132.72) * mm});
            skLineSegment(sketch, "E0.343", {"start": v(122.97, -132.72) * mm, "end": v(131.58, -134.23) * mm});
            skLineSegment(sketch, "E0.344", {"start": v(131.58, -134.23) * mm, "end": v(138.3, -134.73) * mm});
            skLineSegment(sketch, "E0.345", {"start": v(138.3, -134.73) * mm, "end": v(140.5, -134.73) * mm});
            skLineSegment(sketch, "E0.346", {"start": v(140.5, -134.73) * mm, "end": v(141.46, -134.73) * mm});
            skLineSegment(sketch, "E0.347", {"start": v(141.46, -134.73) * mm, "end": v(144.47, -134.53) * mm});
            skLineSegment(sketch, "E0.348", {"start": v(144.47, -134.53) * mm, "end": v(147.93, -133.98) * mm});
            skLineSegment(sketch, "E0.349", {"start": v(147.93, -133.98) * mm, "end": v(150.72, -133.2) * mm});
            skLineSegment(sketch, "E0.350", {"start": v(150.72, -133.2) * mm, "end": v(152.5, -132.43) * mm});
            skLineSegment(sketch, "E0.351", {"start": v(152.5, -132.43) * mm, "end": v(148.75, -131.8) * mm});
            skLineSegment(sketch, "E0.352", {"start": v(148.75, -131.8) * mm, "end": v(144.04, -130.5) * mm});
            skLineSegment(sketch, "E0.353", {"start": v(144.04, -130.5) * mm, "end": v(139.05, -128.61) * mm});
            skLineSegment(sketch, "E0.354", {"start": v(139.05, -128.61) * mm, "end": v(133.76, -126.14) * mm});
            skLineSegment(sketch, "E0.355", {"start": v(133.76, -126.14) * mm, "end": v(128.19, -123.04) * mm});
            skLineSegment(sketch, "E0.356", {"start": v(128.19, -123.04) * mm, "end": v(123.72, -120.24) * mm});
            skLineSegment(sketch, "E0.357", {"start": v(123.72, -120.24) * mm, "end": v(122.25, -119.25) * mm});
            skLineSegment(sketch, "E0.358", {"start": v(122.25, -119.25) * mm, "end": v(120.03, -117.74) * mm});
            skLineSegment(sketch, "E0.359", {"start": v(120.03, -117.74) * mm, "end": v(113.45, -113.17) * mm});
            skLineSegment(sketch, "E0.360", {"start": v(113.45, -113.17) * mm, "end": v(106.17, -107.93) * mm});
            skLineSegment(sketch, "E0.361", {"start": v(106.17, -107.93) * mm, "end": v(100.1, -103.38) * mm});
            skLineSegment(sketch, "E0.362", {"start": v(100.1, -103.38) * mm, "end": v(95, -99.37) * mm});
            skLineSegment(sketch, "E0.363", {"start": v(95, -99.37) * mm, "end": v(90.63, -95.8) * mm});
            skLineSegment(sketch, "E0.364", {"start": v(90.63, -95.8) * mm, "end": v(86.71, -92.54) * mm});
            skLineSegment(sketch, "E0.365", {"start": v(86.71, -92.54) * mm, "end": v(83, -89.46) * mm});
            skLineSegment(sketch, "E0.366", {"start": v(83, -89.46) * mm, "end": v(80.16, -87.16) * mm});
            skLineSegment(sketch, "E0.367", {"start": v(80.16, -87.16) * mm, "end": v(75.26, -83.32) * mm});
            skLineSegment(sketch, "E0.368", {"start": v(75.26, -83.32) * mm, "end": v(79.1, -76.93) * mm});
            skLineSegment(sketch, "E0.369", {"start": v(79.1, -76.93) * mm, "end": v(82.66, -70.52) * mm});
            skLineSegment(sketch, "E0.370", {"start": v(82.66, -70.52) * mm, "end": v(86.66, -62.51) * mm});
            skLineSegment(sketch, "E0.371", {"start": v(86.66, -62.51) * mm, "end": v(89.9, -55.01) * mm});
            skLineSegment(sketch, "E0.372", {"start": v(89.9, -55.01) * mm, "end": v(92.5, -47.96) * mm});
            skLineSegment(sketch, "E0.373", {"start": v(92.5, -47.96) * mm, "end": v(94.54, -41.31) * mm});
            skLineSegment(sketch, "E0.374", {"start": v(94.54, -41.31) * mm, "end": v(96.13, -35.02) * mm});
            skLineSegment(sketch, "E0.375", {"start": v(96.13, -35.02) * mm, "end": v(97.34, -29.04) * mm});
            skLineSegment(sketch, "E0.376", {"start": v(97.34, -29.04) * mm, "end": v(98.27, -23.33) * mm});
            skLineSegment(sketch, "E0.377", {"start": v(98.27, -23.33) * mm, "end": v(99, -17.82) * mm});
            skLineSegment(sketch, "E0.378", {"start": v(99, -17.82) * mm, "end": v(99.63, -12.48) * mm});
            skLineSegment(sketch, "E0.379", {"start": v(99.63, -12.48) * mm, "end": v(100.24, -7.26) * mm});
            skLineSegment(sketch, "E0.380", {"start": v(100.24, -7.26) * mm, "end": v(100.92, -2.12) * mm});
            skLineSegment(sketch, "E0.381", {"start": v(100.92, -2.12) * mm, "end": v(101.78, 2.98) * mm});
            skLineSegment(sketch, "E0.382", {"start": v(101.78, 2.98) * mm, "end": v(102.91, 8.06) * mm});
            skLineSegment(sketch, "E0.383", {"start": v(102.91, 8.06) * mm, "end": v(104.41, 13.1) * mm});
            skLineSegment(sketch, "E0.384", {"start": v(104.41, 13.1) * mm, "end": v(105.85, 16.93) * mm});
            skLineSegment(sketch, "E0.385", {"start": v(105.85, 16.93) * mm, "end": v(106.42, 18.2) * mm});
            skLineSegment(sketch, "E0.386", {"start": v(106.42, 18.2) * mm, "end": v(106.77, 18.98) * mm});
            skLineSegment(sketch, "E0.387", {"start": v(106.77, 18.98) * mm, "end": v(108.01, 21.06) * mm});
            skLineSegment(sketch, "E0.388", {"start": v(108.01, 21.06) * mm, "end": v(110.27, 23.64) * mm});
            skLineSegment(sketch, "E0.389", {"start": v(110.27, 23.64) * mm, "end": v(113.32, 25.87) * mm});
            skLineSegment(sketch, "E0.390", {"start": v(113.32, 25.87) * mm, "end": v(116.23, 27.32) * mm});
            skLineSegment(sketch, "E0.391", {"start": v(116.23, 27.32) * mm, "end": v(117.32, 27.72) * mm});
            skLineSegment(sketch, "E0.392", {"start": v(117.32, 27.72) * mm, "end": v(117.87, 27.92) * mm});
            skLineSegment(sketch, "E0.393", {"start": v(117.87, 27.92) * mm, "end": v(119.4, 28.66) * mm});
            skLineSegment(sketch, "E0.394", {"start": v(119.4, 28.66) * mm, "end": v(120.18, 29.26) * mm});
            skLineSegment(sketch, "E0.395", {"start": v(120.18, 29.26) * mm, "end": v(120.14, 29.26) * mm});
            skLineSegment(sketch, "E0.396", {"start": v(120.14, 29.26) * mm, "end": v(120.04, 29.26) * mm});
            skLineSegment(sketch, "E0.397", {"start": v(120.04, 29.26) * mm, "end": v(119.38, 29.21) * mm});
            skLineSegment(sketch, "E0.398", {"start": v(119.38, 29.21) * mm, "end": v(117.41, 29.06) * mm});
            skLineSegment(sketch, "E0.399", {"start": v(117.41, 29.06) * mm, "end": v(114.6, 28.83) * mm});
            skLineSegment(sketch, "E0.400", {"start": v(114.6, 28.83) * mm, "end": v(110.98, 28.56) * mm});
            skLineSegment(sketch, "E0.401", {"start": v(110.98, 28.56) * mm, "end": v(106.62, 28.3) * mm});
            skLineSegment(sketch, "E0.402", {"start": v(106.62, 28.3) * mm, "end": v(101.56, 28.07) * mm});
            skLineSegment(sketch, "E0.403", {"start": v(101.56, 28.07) * mm, "end": v(95.84, 27.9) * mm});
            skLineSegment(sketch, "E0.404", {"start": v(95.84, 27.9) * mm, "end": v(91.06, 27.84) * mm});
            skLineSegment(sketch, "E0.405", {"start": v(91.06, 27.84) * mm, "end": v(89.46, 27.84) * mm});
            skLineSegment(sketch, "E0.406", {"start": v(89.46, 27.84) * mm, "end": v(87.41, 27.84) * mm});
            skLineSegment(sketch, "E0.407", {"start": v(87.41, 27.84) * mm, "end": v(81.3, 27.9) * mm});
            skSolve(sketch);
        }
        {
            var Q0;
            Q0=makeQuery(id+"F0.imprint","IMPRINT",FACE,{"disambiguationData":[TD([[makeQuery(id+"F0.imprint","IMPRINT",EDGE,{"derivedFrom":sQuery(id+"F0.wireOp",EDGE,"E0.0")}),1.0]])]});
            extrude(context, id + "F1", {"entities" : qUnion([Q0]), "depth" : 2 * mm});
        }
    });
